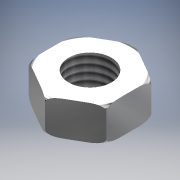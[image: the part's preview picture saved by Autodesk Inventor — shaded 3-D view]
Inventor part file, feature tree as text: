
AUTODESK INVENTOR PART (.ipt)
format: ipt  version: 2017 (Build 210142000, 142)  size: 162,816 bytes
history: native  units: in
note: dims shown in document units (in); Inventor stores cm internally (conversion verified against a paired STEP export)
features: other x3, sketch x2, extrude x1, thread x1, plane x1, revolve x1, mirror x1
ambient origin geometry x8: Origin, YZ Plane, XZ Plane, XY Plane, X Axis, Y Axis, Z Axis, Center Point
bodies: Solid1 (feature_tree)
feature tree (10):
  extrude  "Extrusion1"  Depth=0.095in TaperAngle=0.0deg
  thread  "Thread1"  [1 undecoded]
  sketch  "Sketch3"  dims[d8=0.015in d9=90.0deg]
  other  "Work Point1"
  other  "Work Point2"
  other  "Work Point3"
  plane  "Work Plane1"
  revolve  "Revolution2"  Angle=90.0deg
  mirror  "Mirror1"
  sketch  "Sketch1"  dims[d1=0.1181in d2=0.095in d3=0.0in d4=1.0in d5=0.0in]
note: 1 required parameter value undecoded (feature->parameter linkage not recoverable at this tier; creation-order binding heuristic only, values carry confidence <= 0.55)
